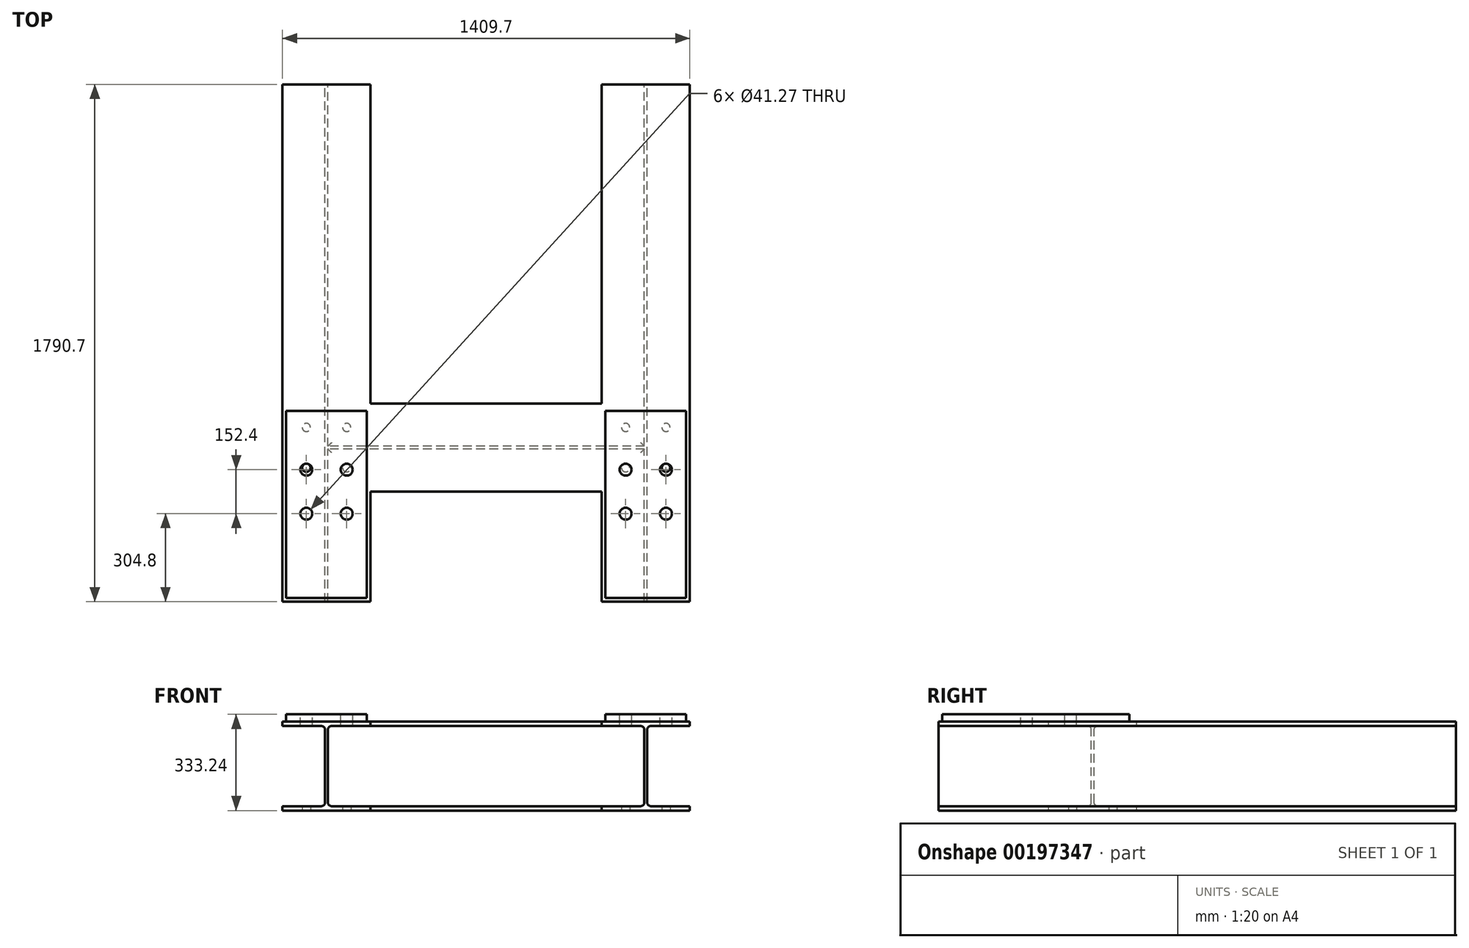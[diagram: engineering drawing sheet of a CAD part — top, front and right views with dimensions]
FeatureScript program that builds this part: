
annotation { "Feature Type Name" : "Feature", "Feature Type Description" : "" }
export const myFeature = defineFeature(function(context is Context, id is Id, definition is map)
    precondition{}
    {
        {
            var Q0;
            Q0=qCreatedBy(makeId("Front.planeOp"),FACE);
            var sketch = newSketch(context, id + "F0", { "sketchPlane" : qUnion([Q0])});
            skLineSegment(sketch, "E0", {"start": v(0, 114) * mm, "end": v(0, -107.16) * mm, "construction": true});
            skLineSegment(sketch, "E1", {"start": v(-552.45, 0) * mm, "end": v(148.25, 0) * mm, "construction": true});
            skLineSegment(sketch, "E2.0", {"start": v(-552.45, 138.68) * mm, "end": v(-552.45, -138.68) * mm, "construction": true});
            skPoint(sketch, "E3.orphan", {"position": v(-150.99, 0) * mm});
            skLineSegment(sketch, "E4.bottom", {"start": v(-704.85, 153.92) * mm, "end": v(-400.05, 153.92) * mm});
            skLineSegment(sketch, "E4.top", {"start": v(-704.85, -153.92) * mm, "end": v(-400.05, -153.92) * mm});
            skLineSegment(sketch, "E4.left", {"start": v(-704.85, 153.92) * mm, "end": v(-704.85, 138.68) * mm});
            skLineSegment(sketch, "E4.right", {"start": v(-400.05, 153.92) * mm, "end": v(-400.05, 138.68) * mm});
            skPoint(sketch, "E4.middle", {"position": v(-552.45, 0) * mm});
            skLineSegment(sketch, "E5.0", {"start": v(-704.85, 138.68) * mm, "end": v(-570.1, 138.68) * mm});
            skLineSegment(sketch, "E6.0", {"start": v(-704.85, -138.68) * mm, "end": v(-570.1, -138.68) * mm});
            skLineSegment(sketch, "E7.0", {"start": v(-557.4, 125.98) * mm, "end": v(-557.4, -125.98) * mm});
            skLineSegment(sketch, "E8.MirrorCS", {"start": v(-547.5, 125.98) * mm, "end": v(-547.5, -125.98) * mm});
            skLineSegment(sketch, "E9.trimOffspring", {"start": v(-534.8, 138.68) * mm, "end": v(-400.05, 138.68) * mm});
            skLineSegment(sketch, "E10.trimOffspring", {"start": v(-534.8, -138.68) * mm, "end": v(-400.05, -138.68) * mm});
            skLineSegment(sketch, "E11.trimOffspring", {"start": v(-704.85, -138.68) * mm, "end": v(-704.85, -153.92) * mm});
            skLineSegment(sketch, "E12.trimOffspring", {"start": v(-400.05, -138.68) * mm, "end": v(-400.05, -153.92) * mm});
            skPoint(sketch, "E13.visualSharp", {"position": v(-557.4, -138.68) * mm});
            skArc(sketch, "E13.filletArc", {"start": v(-570.1, -138.68) * mm, "mid": v(-561.12, -134.96) * mm, "end": v(-557.4, -125.98) * mm});
            skPoint(sketch, "E14.newPointA", {"position": v(-547.5, -138.68) * mm});
            skArc(sketch, "E14.filletArc", {"start": v(-547.5, -125.98) * mm, "mid": v(-543.78, -134.96) * mm, "end": v(-534.8, -138.68) * mm});
            skPoint(sketch, "E15.newPointA", {"position": v(-547.5, 138.68) * mm});
            skArc(sketch, "E15.filletArc", {"start": v(-534.8, 138.68) * mm, "mid": v(-543.78, 134.96) * mm, "end": v(-547.5, 125.98) * mm});
            skPoint(sketch, "E16.visualSharp", {"position": v(-557.4, 138.68) * mm});
            skArc(sketch, "E16.filletArc", {"start": v(-557.4, 125.98) * mm, "mid": v(-561.12, 134.96) * mm, "end": v(-570.1, 138.68) * mm});
            skSolve(sketch);
        }
        {
            var Q0;
            Q0=makeQuery(id+"F0.imprint","IMPRINT",FACE,{"disambiguationData":[TD([[makeQuery(id+"F0.imprint","IMPRINT",EDGE,{"derivedFrom":sQuery(id+"F0.wireOp",EDGE,"E4.bottom")}),-1.0]])]});
            extrude(context, id + "F1", {"entities" : qUnion([Q0]), "endBound" : BoundingType.SYMMETRIC, "depth" : 1790.7 * mm});
        }
        {
            var Q0;
            Q0=makeQuery(id+"F1.opExtrude","SWEPT_FACE",FACE,{"disambiguationData":[OSD([sQuery(id+"F0.wireOp",EDGE,"E4.bottom")])]});
            var sketch = newSketch(context, id + "F2", { "sketchPlane" : qUnion([Q0])});
            skLineSegment(sketch, "E17.0", {"start": v(-692.15, -882.65) * mm, "end": v(-412.75, -882.65) * mm});
            skLineSegment(sketch, "E18.0", {"start": v(-692.15, -234.95) * mm, "end": v(-412.75, -234.95) * mm});
            skLineSegment(sketch, "E19", {"start": v(-552.45, 895.35) * mm, "end": v(-552.45, -1029.61) * mm, "construction": true});
            skLineSegment(sketch, "E20.0", {"start": v(-692.15, -234.95) * mm, "end": v(-692.15, -882.65) * mm});
            skLineSegment(sketch, "E21.MirrorCS", {"start": v(-412.75, -234.95) * mm, "end": v(-412.75, -882.65) * mm});
            skSolve(sketch);
        }
        {
            var Q0;
            Q0 = qSketchRegion(id + "F2", true);
            extrude(context, id + "F3", {"entities" : qUnion([Q0]), "operationType" : NewBodyOperationType.ADD, "depth" : 25.4 * mm});
        }
        {
            var Q0;
            Q0=makeQuery(id+"F3.opExtrude","CAP_FACE",FACE,{"disambiguationData":[OSD([sQuery(id+"F2.wireOp",EDGE,"E17.0"),sQuery(id+"F2.wireOp",EDGE,"E18.0"),sQuery(id+"F2.wireOp",EDGE,"E20.0"),sQuery(id+"F2.wireOp",EDGE,"E21.MirrorCS")])],"isStart":false});
            var sketch = newSketch(context, id + "F4", { "sketchPlane" : qUnion([Q0])});
            skLineSegment(sketch, "E22.0", {"start": v(-704.85, -590.55) * mm, "end": v(-400.05, -590.55) * mm, "construction": true});
            skLineSegment(sketch, "E23.0", {"start": v(-704.85, -438.15) * mm, "end": v(-400.05, -438.15) * mm, "construction": true});
            skLineSegment(sketch, "E24.0", {"start": v(-704.85, -895.35) * mm, "end": v(-400.05, -895.35) * mm, "construction": true});
            skLineSegment(sketch, "E25", {"start": v(-552.45, -895.35) * mm, "end": v(-552.45, -353.42) * mm, "construction": true});
            skLineSegment(sketch, "E26.0", {"start": v(-482.6, -895.35) * mm, "end": v(-482.6, -353.42) * mm, "construction": true});
            skPoint(sketch, "E27", {"position": v(-482.6, -438.15) * mm});
            skPoint(sketch, "E28", {"position": v(-482.6, -590.55) * mm});
            skPoint(sketch, "E29.MirrorP", {"position": v(-622.3, -438.15) * mm});
            skPoint(sketch, "E30.MirrorP", {"position": v(-622.3, -590.55) * mm});
            skSolve(sketch);
        }
        {
            var Q0;
            Q0=sQuery(id+"F4.wireOp",VERTEX,"E29.MirrorP");
            var Q1;
            Q1=sQuery(id+"F4.wireOp",VERTEX,"E27");
            var Q2;
            Q2=sQuery(id+"F4.wireOp",VERTEX,"E30.MirrorP");
            var Q3;
            Q3=sQuery(id+"F4.wireOp",VERTEX,"E28");
            var Q4;
            Q4=makeQuery(id+"F1.opExtrude","SWEPT_BODY",BODY,{"disambiguationData":[OSD([sQuery(id+"F0.wireOp",EDGE,"E4.bottom"),sQuery(id+"F0.wireOp",EDGE,"E4.top"),sQuery(id+"F0.wireOp",EDGE,"E4.left"),sQuery(id+"F0.wireOp",EDGE,"E4.right"),sQuery(id+"F0.wireOp",EDGE,"E5.0"),sQuery(id+"F0.wireOp",EDGE,"E6.0"),sQuery(id+"F0.wireOp",EDGE,"E7.0"),sQuery(id+"F0.wireOp",EDGE,"E8.MirrorCS"),sQuery(id+"F0.wireOp",EDGE,"E9.trimOffspring"),sQuery(id+"F0.wireOp",EDGE,"E10.trimOffspring"),sQuery(id+"F0.wireOp",EDGE,"E11.trimOffspring"),sQuery(id+"F0.wireOp",EDGE,"E12.trimOffspring"),sQuery(id+"F0.wireOp",EDGE,"E13.filletArc"),sQuery(id+"F0.wireOp",EDGE,"E14.filletArc"),sQuery(id+"F0.wireOp",EDGE,"E15.filletArc"),sQuery(id+"F0.wireOp",EDGE,"E16.filletArc")])]});
            hole(context, id + "F5", {"style" : HoleStyle.SIMPLE, "endStyle" : HoleEndStyle.BLIND, "holeDiameter" : 41.27 * mm, "holeDepth" : 76.2 * mm, "locations" : qUnion([Q0, Q1, Q2, Q3]), "scope" : qUnion([Q4])});
        }
        {
            var Q0;
            Q0=makeQuery(id+"F1.opExtrude","SWEPT_FACE",FACE,{"disambiguationData":[OSD([sQuery(id+"F0.wireOp",EDGE,"E4.top")])]});
            var sketch = newSketch(context, id + "F6", { "sketchPlane" : qUnion([Q0])});
            skLineSegment(sketch, "E31.0", {"start": v(-704.85, 895.35) * mm, "end": v(-400.05, 895.35) * mm, "construction": true});
            skLineSegment(sketch, "E32.0", {"start": v(-704.85, 361.95) * mm, "end": v(-400.05, 361.95) * mm, "construction": true});
            skLineSegment(sketch, "E33.0", {"start": v(-704.85, 292.1) * mm, "end": v(-400.05, 292.1) * mm, "construction": true});
            skLineSegment(sketch, "E34", {"start": v(-552.45, 895.35) * mm, "end": v(-552.45, 107.68) * mm, "construction": true});
            skLineSegment(sketch, "E35.0", {"start": v(-622.3, 895.35) * mm, "end": v(-622.3, 107.68) * mm, "construction": true});
            skPoint(sketch, "E36", {"position": v(-622.3, 292.1) * mm});
            skPoint(sketch, "E37.MirrorP", {"position": v(-482.6, 292.1) * mm});
            skPoint(sketch, "E38.MirrorP", {"position": v(-482.6, 431.8) * mm});
            skPoint(sketch, "E39.MirrorP", {"position": v(-622.3, 431.8) * mm});
            skSolve(sketch);
        }
        {
            var Q0;
            Q0=sQuery(id+"F6.wireOp",VERTEX,"E38.MirrorP");
            var Q1;
            Q1=sQuery(id+"F6.wireOp",VERTEX,"E37.MirrorP");
            var Q2;
            Q2=sQuery(id+"F6.wireOp",VERTEX,"E39.MirrorP");
            var Q3;
            Q3=sQuery(id+"F6.wireOp",VERTEX,"E36");
            var Q4;
            Q4=makeQuery(id+"F1.opExtrude","SWEPT_BODY",BODY,{"disambiguationData":[OSD([sQuery(id+"F0.wireOp",EDGE,"E4.bottom"),sQuery(id+"F0.wireOp",EDGE,"E4.top"),sQuery(id+"F0.wireOp",EDGE,"E4.left"),sQuery(id+"F0.wireOp",EDGE,"E4.right"),sQuery(id+"F0.wireOp",EDGE,"E5.0"),sQuery(id+"F0.wireOp",EDGE,"E6.0"),sQuery(id+"F0.wireOp",EDGE,"E7.0"),sQuery(id+"F0.wireOp",EDGE,"E8.MirrorCS"),sQuery(id+"F0.wireOp",EDGE,"E9.trimOffspring"),sQuery(id+"F0.wireOp",EDGE,"E10.trimOffspring"),sQuery(id+"F0.wireOp",EDGE,"E11.trimOffspring"),sQuery(id+"F0.wireOp",EDGE,"E12.trimOffspring"),sQuery(id+"F0.wireOp",EDGE,"E13.filletArc"),sQuery(id+"F0.wireOp",EDGE,"E14.filletArc"),sQuery(id+"F0.wireOp",EDGE,"E15.filletArc"),sQuery(id+"F0.wireOp",EDGE,"E16.filletArc")])]});
            hole(context, id + "F7", {"style" : HoleStyle.SIMPLE, "endStyle" : HoleEndStyle.BLIND, "holeDiameter" : 28.57 * mm, "holeDepth" : 76.2 * mm, "locations" : qUnion([Q0, Q1, Q2, Q3]), "scope" : qUnion([Q4])});
        }
        {
            var Q0;
            Q0=makeQuery(id+"F1.opExtrude","SWEPT_BODY",BODY,{"disambiguationData":[OSD([sQuery(id+"F0.wireOp",EDGE,"E4.bottom"),sQuery(id+"F0.wireOp",EDGE,"E4.top"),sQuery(id+"F0.wireOp",EDGE,"E4.left"),sQuery(id+"F0.wireOp",EDGE,"E4.right"),sQuery(id+"F0.wireOp",EDGE,"E5.0"),sQuery(id+"F0.wireOp",EDGE,"E6.0"),sQuery(id+"F0.wireOp",EDGE,"E7.0"),sQuery(id+"F0.wireOp",EDGE,"E8.MirrorCS"),sQuery(id+"F0.wireOp",EDGE,"E9.trimOffspring"),sQuery(id+"F0.wireOp",EDGE,"E10.trimOffspring"),sQuery(id+"F0.wireOp",EDGE,"E11.trimOffspring"),sQuery(id+"F0.wireOp",EDGE,"E12.trimOffspring"),sQuery(id+"F0.wireOp",EDGE,"E13.filletArc"),sQuery(id+"F0.wireOp",EDGE,"E14.filletArc"),sQuery(id+"F0.wireOp",EDGE,"E15.filletArc"),sQuery(id+"F0.wireOp",EDGE,"E16.filletArc")])]});
            var Q1;
            Q1=qCreatedBy(makeId("Right.planeOp"),FACE);
            mirror(context, id + "F8", {"entities" : qUnion([Q0]), "mirrorPlane" : qUnion([Q1])});
        }
        {
            var Q0;
            Q0=qCreatedBy(makeId("Right.planeOp"),FACE);
            var sketch = newSketch(context, id + "F9", { "sketchPlane" : qUnion([Q0])});
            skLineSegment(sketch, "E40.0", {"start": v(-895.35, 488.96) * mm, "end": v(-895.35, -443.79) * mm, "construction": true});
            skPoint(sketch, "E41.orphan", {"position": v(-895.35, 125.98) * mm});
            skPoint(sketch, "E42.orphan", {"position": v(-895.35, -125.98) * mm});
            skLineSegment(sketch, "E43.0", {"start": v(895.35, 125.98) * mm, "end": v(895.35, -125.98) * mm, "construction": true});
            skLineSegment(sketch, "E44", {"start": v(988.1, 0) * mm, "end": v(-1115.09, 0) * mm, "construction": true});
            skPoint(sketch, "E44.startSnap0", {"position": v(895.35, 0) * mm});
            skPoint(sketch, "E44.endSnap0", {"position": v(895.35, 0) * mm});
            skLineSegment(sketch, "E45.0", {"start": v(-361.95, 488.96) * mm, "end": v(-361.95, -138.68) * mm, "construction": true});
            skLineSegment(sketch, "E46.0", {"start": v(-895.35, 153.92) * mm, "end": v(895.35, 153.92) * mm, "construction": true});
            skLineSegment(sketch, "E47.0", {"start": v(-895.35, -153.92) * mm, "end": v(895.35, -153.92) * mm, "construction": true});
            skLineSegment(sketch, "E48.bottom", {"start": v(-514.35, 153.92) * mm, "end": v(-209.55, 153.92) * mm});
            skLineSegment(sketch, "E48.top", {"start": v(-514.35, -153.92) * mm, "end": v(-209.55, -153.92) * mm});
            skLineSegment(sketch, "E48.left", {"start": v(-514.35, 153.92) * mm, "end": v(-514.35, 138.68) * mm});
            skLineSegment(sketch, "E48.right", {"start": v(-209.55, 153.92) * mm, "end": v(-209.55, 138.68) * mm});
            skPoint(sketch, "E48.middle", {"position": v(-361.95, 0) * mm});
            skLineSegment(sketch, "E49.0", {"start": v(-895.35, 138.68) * mm, "end": v(-379.6, 138.68) * mm});
            skLineSegment(sketch, "E50.0", {"start": v(-895.35, -138.68) * mm, "end": v(-379.6, -138.68) * mm});
            skLineSegment(sketch, "E51.0", {"start": v(-366.9, 125.98) * mm, "end": v(-366.9, -125.98) * mm});
            skLineSegment(sketch, "E52.MirrorCS", {"start": v(-357, 125.98) * mm, "end": v(-357, -125.98) * mm});
            skPoint(sketch, "E53.orphan", {"position": v(-366.9, 488.96) * mm});
            skPoint(sketch, "E54.orphan", {"position": v(-357, 488.96) * mm});
            skLineSegment(sketch, "E55.trimOffspring", {"start": v(-344.3, 138.68) * mm, "end": v(895.35, 138.68) * mm});
            skPoint(sketch, "E56.orphan", {"position": v(-357, -443.79) * mm});
            skPoint(sketch, "E57.orphan", {"position": v(-366.9, -443.79) * mm});
            skLineSegment(sketch, "E58.trimOffspring", {"start": v(-361.95, -153.92) * mm, "end": v(-361.95, -443.79) * mm, "construction": true});
            skLineSegment(sketch, "E59.trimOffspring", {"start": v(-344.3, -138.68) * mm, "end": v(895.35, -138.68) * mm});
            skPoint(sketch, "E60.visualSharp", {"position": v(-366.9, 138.68) * mm});
            skArc(sketch, "E60.filletArc", {"start": v(-366.9, 125.98) * mm, "mid": v(-370.62, 134.96) * mm, "end": v(-379.6, 138.68) * mm});
            skArc(sketch, "E61.filletArc", {"start": v(-344.3, 138.68) * mm, "mid": v(-353.28, 134.96) * mm, "end": v(-357, 125.98) * mm});
            skPoint(sketch, "E62.visualSharp", {"position": v(-366.9, -138.68) * mm});
            skArc(sketch, "E62.filletArc", {"start": v(-379.6, -138.68) * mm, "mid": v(-370.62, -134.96) * mm, "end": v(-366.9, -125.98) * mm});
            skPoint(sketch, "E63.visualSharp", {"position": v(-357, -138.68) * mm});
            skArc(sketch, "E63.filletArc", {"start": v(-357, -125.98) * mm, "mid": v(-353.28, -134.96) * mm, "end": v(-344.3, -138.68) * mm});
            skLineSegment(sketch, "E64.trimOffspring", {"start": v(-514.35, -138.68) * mm, "end": v(-514.35, -153.92) * mm});
            skLineSegment(sketch, "E65.trimOffspring", {"start": v(-209.55, -138.68) * mm, "end": v(-209.55, -153.92) * mm});
            skSolve(sketch);
        }
        {
            var Q0;
            Q0 = qSketchRegion(id + "F9", true);
            extrude(context, id + "F10", {"entities" : qUnion([Q0]), "operationType" : NewBodyOperationType.ADD, "endBound" : BoundingType.SYMMETRIC, "depth" : 1104.9 * mm});
        }
        {
            var Q0;
            {var subQ0=makeQuery(id+"F1.opExtrude","SWEPT_FACE",FACE,{"disambiguationData":[OSD([sQuery(id+"F0.wireOp",EDGE,"E4.top")])]});Q0=makeQuery(id+"F10.boolean.opBoolean","MERGE",FACE,{"derivedFrom":[subQ0,makeQuery(id+"F8.opPattern","COPY",FACE,{"derivedFrom":subQ0,"instanceName":"1"}),makeQuery(id+"F10.opExtrude","SWEPT_FACE",FACE,{"disambiguationData":[OSD([sQuery(id+"F9.wireOp",EDGE,"E48.top")])]})]});}
            var sketch = newSketch(context, id + "F11", { "sketchPlane" : qUnion([Q0])});
            skLineSegment(sketch, "E66.0", {"start": v(-704.85, 895.35) * mm, "end": v(-400.05, 895.35) * mm, "construction": true});
            skLineSegment(sketch, "E67.0", {"start": v(704.85, 895.35) * mm, "end": v(400.05, 895.35) * mm, "construction": true});
            skLineSegment(sketch, "E68", {"start": v(0, 1041.07) * mm, "end": v(0, -409.2) * mm, "construction": true});
            skLineSegment(sketch, "E69", {"start": v(-552.45, 895.35) * mm, "end": v(-552.45, -102.3) * mm, "construction": true});
            skCircle(sketch, "E70.0", {"center": v(-622.3, 431.8) * mm, "radius": 14.29 * mm, "construction": true});
            skCircle(sketch, "E71.0", {"center": v(-622.3, 292.1) * mm, "radius": 14.29 * mm, "construction": true});
            skCircle(sketch, "E72.MirrorC", {"center": v(-482.6, 431.8) * mm, "radius": 14.29 * mm});
            skCircle(sketch, "E73.MirrorC", {"center": v(-482.6, 292.1) * mm, "radius": 14.29 * mm});
            skCircle(sketch, "E74.MirrorC", {"center": v(482.6, 431.8) * mm, "radius": 14.29 * mm});
            skCircle(sketch, "E75.MirrorC", {"center": v(482.6, 292.1) * mm, "radius": 14.29 * mm});
            skSolve(sketch);
        }
        {
            var Q0;
            Q0 = qSketchRegion(id + "F11", true);
            extrude(context, id + "F12", {"entities" : qUnion([Q0]), "operationType" : NewBodyOperationType.REMOVE, "oppositeDirection" : true, "depth" : 76.2 * mm});
        }
    });
